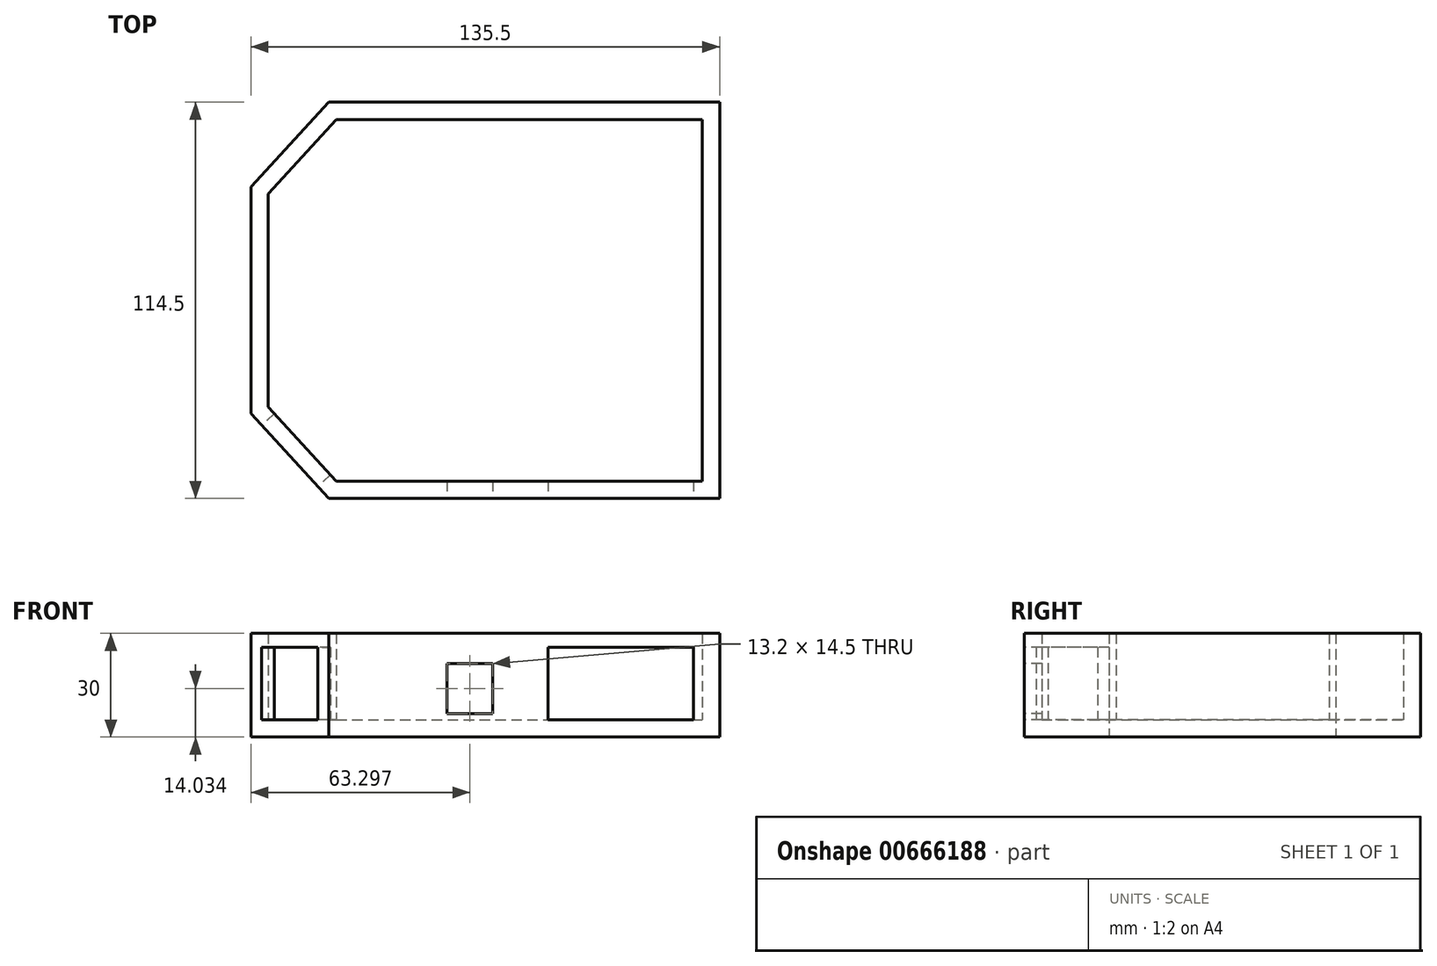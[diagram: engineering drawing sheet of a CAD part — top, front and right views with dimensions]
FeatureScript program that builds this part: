
annotation { "Feature Type Name" : "Feature", "Feature Type Description" : "" }
export const myFeature = defineFeature(function(context is Context, id is Id, definition is map)
    precondition{}
    {
        {
            var Q0;
            Q0=qCreatedBy(makeId("Top.planeOp"),FACE);
            var sketch = newSketch(context, id + "F0", { "sketchPlane" : qUnion([Q0])});
            skLineSegment(sketch, "E0.bottom", {"start": v(44.58, 49.08) * mm, "end": v(-68.42, 49.08) * mm});
            skLineSegment(sketch, "E0.top", {"start": v(44.58, -65.42) * mm, "end": v(-68.42, -65.42) * mm});
            skLineSegment(sketch, "E0.left", {"start": v(44.58, 49.08) * mm, "end": v(44.58, -65.42) * mm});
            skLineSegment(sketch, "E0.right", {"start": v(-90.92, 24.58) * mm, "end": v(-90.92, -40.92) * mm});
            skLineSegment(sketch, "E1", {"start": v(-90.92, -40.92) * mm, "end": v(-68.42, -65.42) * mm});
            skLineSegment(sketch, "E2", {"start": v(-68.42, 49.08) * mm, "end": v(-90.92, 24.58) * mm});
            skPoint(sketch, "E3.orphan", {"position": v(-90.92, -65.42) * mm});
            skPoint(sketch, "E4.orphan", {"position": v(-90.92, 49.08) * mm});
            skSolve(sketch);
        }
        {
            var Q0;
            Q0=makeQuery(id+"F0.imprint","IMPRINT",FACE,{"disambiguationData":[TD([[makeQuery(id+"F0.imprint","IMPRINT",EDGE,{"derivedFrom":sQuery(id+"F0.wireOp",EDGE,"E0.bottom")}),1.0]])]});
            extrude(context, id + "F1", {"entities" : qUnion([Q0]), "depth" : 5 * mm, "offsetDistance" : 25 * mm});
        }
        {
            var Q0;
            Q0=makeQuery(id+"F1.opExtrude","CAP_FACE",FACE,{"disambiguationData":[OSD([sQuery(id+"F0.wireOp",EDGE,"E0.bottom"),sQuery(id+"F0.wireOp",EDGE,"E0.top"),sQuery(id+"F0.wireOp",EDGE,"E0.left"),sQuery(id+"F0.wireOp",EDGE,"E0.right"),sQuery(id+"F0.wireOp",EDGE,"E1"),sQuery(id+"F0.wireOp",EDGE,"E2")])],"isStart":false});
            var sketch = newSketch(context, id + "F2", { "sketchPlane" : qUnion([Q0])});
            skLineSegment(sketch, "E5.0", {"start": v(-66.23, 44.08) * mm, "end": v(-85.92, 22.63) * mm});
            skLineSegment(sketch, "E5.1", {"start": v(-85.92, -38.97) * mm, "end": v(-66.23, -60.42) * mm});
            skLineSegment(sketch, "E5.2", {"start": v(-66.23, -60.42) * mm, "end": v(39.58, -60.42) * mm});
            skLineSegment(sketch, "E5.3", {"start": v(-85.92, 22.63) * mm, "end": v(-85.92, -38.97) * mm});
            skLineSegment(sketch, "E5.4", {"start": v(39.58, -60.42) * mm, "end": v(39.58, 44.08) * mm});
            skLineSegment(sketch, "E5.5", {"start": v(39.58, 44.08) * mm, "end": v(-66.23, 44.08) * mm});
            skSolve(sketch);
        }
        {
            var Q0;
            Q0=makeQuery(id+"F2.imprint","IMPRINT",FACE,{"disambiguationData":[TD([[makeQuery(id+"F2.imprint","IMPRINT",EDGE,{"derivedFrom":sQuery(id+"F2.wireOp",EDGE,"E5.0")}),-1.0]])]});
            extrude(context, id + "F3", {"entities" : qUnion([Q0]), "operationType" : NewBodyOperationType.ADD, "depth" : 25 * mm, "offsetDistance" : 25 * mm});
        }
        {
            var Q0;
            {var subQ0=sQuery(id+"F0.wireOp",EDGE,"E0.top");Q0=makeQuery(id+"F3.boolean.opBoolean","MERGE",FACE,{"derivedFrom":[makeQuery(id+"F1.opExtrude","SWEPT_FACE",FACE,{"disambiguationData":[OSD([subQ0])]}),makeQuery(id+"F3.opExtrude","SWEPT_FACE",FACE,{"disambiguationData":[OSD([subQ0])]})]});}
            var sketch = newSketch(context, id + "F4", { "sketchPlane" : qUnion([Q0])});
            skLineSegment(sketch, "E6.bottom", {"start": v(-34.22, 6.78) * mm, "end": v(-21.02, 6.78) * mm});
            skLineSegment(sketch, "E6.top", {"start": v(-34.22, 21.28) * mm, "end": v(-21.02, 21.28) * mm});
            skLineSegment(sketch, "E6.left", {"start": v(-34.22, 6.78) * mm, "end": v(-34.22, 21.28) * mm});
            skLineSegment(sketch, "E6.right", {"start": v(-21.02, 6.78) * mm, "end": v(-21.02, 21.28) * mm});
            skLineSegment(sketch, "E7.bottom", {"start": v(-5.02, 5) * mm, "end": v(36.98, 5) * mm});
            skLineSegment(sketch, "E7.top", {"start": v(-5.02, 26) * mm, "end": v(36.98, 26) * mm});
            skLineSegment(sketch, "E7.left", {"start": v(-5.02, 5) * mm, "end": v(-5.02, 26) * mm});
            skLineSegment(sketch, "E7.right", {"start": v(36.98, 5) * mm, "end": v(36.98, 26) * mm});
            skSolve(sketch);
        }
        {
            var Q0;
            Q0 = qSketchRegion(id + "F4", true);
            extrude(context, id + "F5", {"entities" : qUnion([Q0]), "operationType" : NewBodyOperationType.REMOVE, "oppositeDirection" : true, "depth" : 25 * mm, "offsetDistance" : 25 * mm});
        }
        {
            var Q0;
            {var subQ0=sQuery(id+"F0.wireOp",EDGE,"E1");Q0=makeQuery(id+"F3.boolean.opBoolean","MERGE",FACE,{"derivedFrom":[makeQuery(id+"F1.opExtrude","SWEPT_FACE",FACE,{"disambiguationData":[OSD([subQ0])]}),makeQuery(id+"F3.opExtrude","SWEPT_FACE",FACE,{"disambiguationData":[OSD([subQ0])]})]});}
            var sketch = newSketch(context, id + "F6", { "sketchPlane" : qUnion([Q0])});
            skLineSegment(sketch, "E8.bottom", {"start": v(-26.76, 26) * mm, "end": v(-2.76, 26) * mm});
            skLineSegment(sketch, "E8.top", {"start": v(-26.76, 5) * mm, "end": v(-2.76, 5) * mm});
            skLineSegment(sketch, "E8.left", {"start": v(-26.76, 26) * mm, "end": v(-26.76, 5) * mm});
            skLineSegment(sketch, "E8.right", {"start": v(-2.76, 26) * mm, "end": v(-2.76, 5) * mm});
            skSolve(sketch);
        }
        {
            var Q0;
            Q0 = qSketchRegion(id + "F6", true);
            extrude(context, id + "F7", {"entities" : qUnion([Q0]), "operationType" : NewBodyOperationType.REMOVE, "endBound" : BoundingType.UP_TO_NEXT, "oppositeDirection" : true, "depth" : 25 * mm, "offsetDistance" : 25 * mm});
        }
    });
